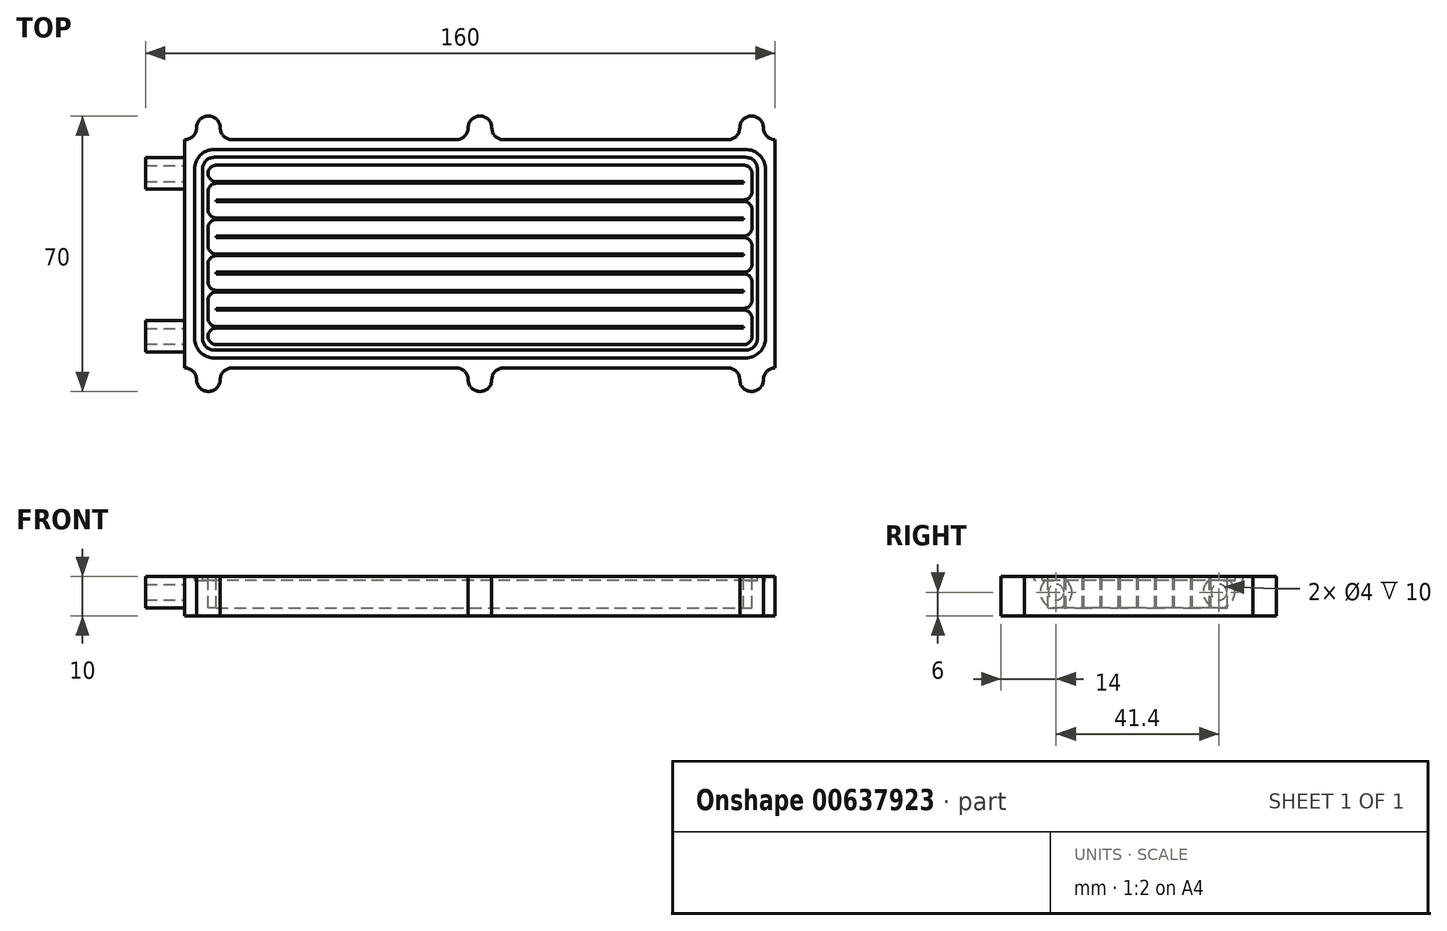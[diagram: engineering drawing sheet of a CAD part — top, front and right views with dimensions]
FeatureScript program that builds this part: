
annotation { "Feature Type Name" : "Feature", "Feature Type Description" : "" }
export const myFeature = defineFeature(function(context is Context, id is Id, definition is map)
    precondition{}
    {
        {
            var Q0;
            Q0=qCreatedBy(makeId("Top.planeOp"),FACE);
            var sketch = newSketch(context, id + "F0", { "sketchPlane" : qUnion([Q0])});
            skLineSegment(sketch, "E0.bottom", {"start": v(63, 29) * mm, "end": v(6, 29) * mm});
            skLineSegment(sketch, "E0.top", {"start": v(63, -29) * mm, "end": v(6, -29) * mm});
            skLineSegment(sketch, "E0.left", {"start": v(75, 29) * mm, "end": v(75, -29) * mm});
            skLineSegment(sketch, "E0.right", {"start": v(-75, 29) * mm, "end": v(-75, -29) * mm});
            skPoint(sketch, "E0.middle", {"position": v(0, 0) * mm});
            skArc(sketch, "E1", {"start": v(3, 32) * mm, "mid": v(0, 35) * mm, "end": v(-3, 32) * mm});
            skArc(sketch, "E2", {"start": v(-66, 32) * mm, "mid": v(-69, 35) * mm, "end": v(-72, 32) * mm});
            skArc(sketch, "E3", {"start": v(72, 32) * mm, "mid": v(69, 35) * mm, "end": v(66, 32) * mm});
            skArc(sketch, "E4", {"start": v(-75, 29) * mm, "mid": v(-72.88, 29.88) * mm, "end": v(-72, 32) * mm});
            skArc(sketch, "E5", {"start": v(-66, 32) * mm, "mid": v(-65.12, 29.88) * mm, "end": v(-63, 29) * mm});
            skArc(sketch, "E6", {"start": v(3, 32) * mm, "mid": v(3.88, 29.88) * mm, "end": v(6, 29) * mm});
            skArc(sketch, "E7", {"start": v(-6, 29) * mm, "mid": v(-3.88, 29.88) * mm, "end": v(-3, 32) * mm});
            skLineSegment(sketch, "E8.trimOffspring", {"start": v(-6, 29) * mm, "end": v(-63, 29) * mm});
            skArc(sketch, "E9", {"start": v(72, 32) * mm, "mid": v(72.88, 29.88) * mm, "end": v(75, 29) * mm});
            skArc(sketch, "E10", {"start": v(63, 29) * mm, "mid": v(65.12, 29.88) * mm, "end": v(66, 32) * mm});
            skArc(sketch, "E11.MirrorCS", {"start": v(-66, -32) * mm, "mid": v(-69, -35) * mm, "end": v(-72, -32) * mm});
            skArc(sketch, "E12.MirrorCS", {"start": v(-75, -29) * mm, "mid": v(-72.88, -29.88) * mm, "end": v(-72, -32) * mm});
            skArc(sketch, "E13.MirrorCS", {"start": v(-66, -32) * mm, "mid": v(-65.12, -29.88) * mm, "end": v(-63, -29) * mm});
            skArc(sketch, "E14.MirrorCS", {"start": v(-6, -29) * mm, "mid": v(-3.88, -29.88) * mm, "end": v(-3, -32) * mm});
            skArc(sketch, "E15.MirrorCS", {"start": v(3, -32) * mm, "mid": v(3.88, -29.88) * mm, "end": v(6, -29) * mm});
            skArc(sketch, "E16.MirrorCS", {"start": v(3, -32) * mm, "mid": v(0, -35) * mm, "end": v(-3, -32) * mm});
            skArc(sketch, "E17.MirrorCS", {"start": v(63, -29) * mm, "mid": v(65.12, -29.88) * mm, "end": v(66, -32) * mm});
            skArc(sketch, "E18.MirrorCS", {"start": v(72, -32) * mm, "mid": v(69, -35) * mm, "end": v(66, -32) * mm});
            skArc(sketch, "E19.MirrorCS", {"start": v(72, -32) * mm, "mid": v(72.88, -29.88) * mm, "end": v(75, -29) * mm});
            skLineSegment(sketch, "E20.trimOffspring", {"start": v(-6, -29) * mm, "end": v(-63, -29) * mm});
            skPoint(sketch, "E21.orphan", {"position": v(-75, 0) * mm});
            skPoint(sketch, "E22.end.orphan", {"position": v(75, 0) * mm});
            skSolve(sketch);
        }
        {
            var Q0;
            Q0=makeQuery(id+"F0.imprint","IMPRINT",FACE,{"disambiguationData":[TD([[makeQuery(id+"F0.imprint","IMPRINT",EDGE,{"derivedFrom":sQuery(id+"F0.wireOp",EDGE,"E0.bottom")}),1.0]])]});
            extrude(context, id + "F1", {"entities" : qUnion([Q0]), "oppositeDirection" : true, "depth" : 10 * mm, "offsetDistance" : 25 * mm});
        }
        {
            var Q0;
            Q0=makeQuery(id+"F1.opExtrude","CAP_FACE",FACE,{"disambiguationData":[OSD([sQuery(id+"F0.wireOp",EDGE,"E0.bottom"),sQuery(id+"F0.wireOp",EDGE,"E0.top"),sQuery(id+"F0.wireOp",EDGE,"E0.left"),sQuery(id+"F0.wireOp",EDGE,"E0.right")])],"isStart":true});
            var sketch = newSketch(context, id + "F2", { "sketchPlane" : qUnion([Q0])});
            skLineSegment(sketch, "E23.bottom", {"start": v(67.5, 26.5) * mm, "end": v(-67.5, 26.5) * mm});
            skLineSegment(sketch, "E23.top", {"start": v(67.5, -26.5) * mm, "end": v(-67.5, -26.5) * mm});
            skLineSegment(sketch, "E23.left", {"start": v(72.5, 21.5) * mm, "end": v(72.5, -21.5) * mm});
            skLineSegment(sketch, "E23.right", {"start": v(-72.5, 21.5) * mm, "end": v(-72.5, -21.5) * mm});
            skPoint(sketch, "E23.middle", {"position": v(0, 0) * mm});
            skPoint(sketch, "E24.visualSharp", {"position": v(-72.5, 26.5) * mm});
            skArc(sketch, "E24.filletArc", {"start": v(-67.5, 26.5) * mm, "mid": v(-71.04, 25.04) * mm, "end": v(-72.5, 21.5) * mm});
            skPoint(sketch, "E25.visualSharp", {"position": v(-72.5, -26.5) * mm});
            skArc(sketch, "E25.filletArc", {"start": v(-72.5, -21.5) * mm, "mid": v(-71.04, -25.04) * mm, "end": v(-67.5, -26.5) * mm});
            skPoint(sketch, "E26.visualSharp", {"position": v(72.5, -26.5) * mm});
            skArc(sketch, "E26.filletArc", {"start": v(67.5, -26.5) * mm, "mid": v(71.04, -25.04) * mm, "end": v(72.5, -21.5) * mm});
            skPoint(sketch, "E27.visualSharp", {"position": v(72.5, 26.5) * mm});
            skArc(sketch, "E27.filletArc", {"start": v(72.5, 21.5) * mm, "mid": v(71.04, 25.04) * mm, "end": v(67.5, 26.5) * mm});
            skLineSegment(sketch, "E28.0", {"start": v(67.5, 24.5) * mm, "end": v(-67.5, 24.5) * mm});
            skLineSegment(sketch, "E28.1", {"start": v(70.5, 21.5) * mm, "end": v(70.5, -21.5) * mm});
            skLineSegment(sketch, "E28.2", {"start": v(67.5, -24.5) * mm, "end": v(-67.5, -24.5) * mm});
            skLineSegment(sketch, "E28.3", {"start": v(-70.5, 21.5) * mm, "end": v(-70.5, -21.5) * mm});
            skPoint(sketch, "E29.visualSharp", {"position": v(-70.5, 24.5) * mm});
            skArc(sketch, "E29.filletArc", {"start": v(-67.5, 24.5) * mm, "mid": v(-69.62, 23.62) * mm, "end": v(-70.5, 21.5) * mm});
            skPoint(sketch, "E30.visualSharp", {"position": v(-70.5, -24.5) * mm});
            skArc(sketch, "E30.filletArc", {"start": v(-70.5, -21.5) * mm, "mid": v(-69.62, -23.62) * mm, "end": v(-67.5, -24.5) * mm});
            skPoint(sketch, "E31.visualSharp", {"position": v(70.5, 24.5) * mm});
            skArc(sketch, "E31.filletArc", {"start": v(70.5, 21.5) * mm, "mid": v(69.62, 23.62) * mm, "end": v(67.5, 24.5) * mm});
            skPoint(sketch, "E32.visualSharp", {"position": v(70.5, -24.5) * mm});
            skArc(sketch, "E32.filletArc", {"start": v(67.5, -24.5) * mm, "mid": v(69.62, -23.62) * mm, "end": v(70.5, -21.5) * mm});
            skSolve(sketch);
        }
        {
            var Q0;
            Q0 = qSketchRegion(id + "F2", true);
            extrude(context, id + "F3", {"entities" : qUnion([Q0]), "operationType" : NewBodyOperationType.REMOVE, "oppositeDirection" : true, "depth" : 1 * mm, "offsetDistance" : 25 * mm});
        }
        {
            var Q0;
            Q0=makeQuery(id+"F3.boolean.opBoolean","SPLIT",FACE,{"disambiguationData":[TD([makeQuery(id+"F3.opExtrude","SWEPT_FACE",FACE,{"disambiguationData":[OSD([sQuery(id+"F2.wireOp",EDGE,"E28.0")])]})])],"derivedFrom":makeQuery(id+"F1.opExtrude","CAP_FACE",FACE,{"disambiguationData":[OSD([sQuery(id+"F0.wireOp",EDGE,"E0.bottom"),sQuery(id+"F0.wireOp",EDGE,"E0.top"),sQuery(id+"F0.wireOp",EDGE,"E0.left"),sQuery(id+"F0.wireOp",EDGE,"E0.right")])],"isStart":true})});
            var sketch = newSketch(context, id + "F4", { "sketchPlane" : qUnion([Q0])});
            skArc(sketch, "E33", {"start": v(-67, -18.9) * mm, "mid": v(-69.1, -21) * mm, "end": v(-67, -23.1) * mm});
            skArc(sketch, "E34", {"start": v(67, -23.1) * mm, "mid": v(68.48, -22.48) * mm, "end": v(69.1, -21) * mm});
            skLineSegment(sketch, "E35", {"start": v(-67, -23.1) * mm, "end": v(67, -23.1) * mm});
            skLineSegment(sketch, "E36", {"start": v(67, -18.9) * mm, "end": v(-67, -18.9) * mm});
            skArc(sketch, "E37.0.1.0", {"start": v(-69.1, -16.4) * mm, "mid": v(-68.48, -17.88) * mm, "end": v(-67, -18.5) * mm});
            skArc(sketch, "E37.0.1.1", {"start": v(69.1, -16.4) * mm, "mid": v(68.48, -14.92) * mm, "end": v(67, -14.3) * mm});
            skLineSegment(sketch, "E37.0.1.2", {"start": v(-67, -18.5) * mm, "end": v(67, -18.5) * mm});
            skLineSegment(sketch, "E37.0.1.3", {"start": v(67, -14.3) * mm, "end": v(-67, -14.3) * mm});
            skArc(sketch, "E37.0.2.0", {"start": v(-67, -9.7) * mm, "mid": v(-68.48, -10.32) * mm, "end": v(-69.1, -11.8) * mm});
            skArc(sketch, "E37.0.2.1", {"start": v(67, -13.9) * mm, "mid": v(68.48, -13.28) * mm, "end": v(69.1, -11.8) * mm});
            skLineSegment(sketch, "E37.0.2.2", {"start": v(-67, -13.9) * mm, "end": v(67, -13.9) * mm});
            skLineSegment(sketch, "E37.0.2.3", {"start": v(67, -9.7) * mm, "end": v(-67, -9.7) * mm});
            skArc(sketch, "E37.0.3.0", {"start": v(-69.1, -7.2) * mm, "mid": v(-68.48, -8.68) * mm, "end": v(-67, -9.3) * mm});
            skArc(sketch, "E37.0.3.1", {"start": v(69.1, -7.2) * mm, "mid": v(68.48, -5.72) * mm, "end": v(67, -5.1) * mm});
            skLineSegment(sketch, "E37.0.3.2", {"start": v(-67, -9.3) * mm, "end": v(67, -9.3) * mm});
            skLineSegment(sketch, "E37.0.3.3", {"start": v(67, -5.1) * mm, "end": v(-67, -5.1) * mm});
            skArc(sketch, "E37.0.4.0", {"start": v(-67, -0.5) * mm, "mid": v(-68.48, -1.12) * mm, "end": v(-69.1, -2.6) * mm});
            skArc(sketch, "E37.0.4.1", {"start": v(67, -4.7) * mm, "mid": v(68.48, -4.08) * mm, "end": v(69.1, -2.6) * mm});
            skLineSegment(sketch, "E37.0.4.2", {"start": v(-67, -4.7) * mm, "end": v(67, -4.7) * mm});
            skLineSegment(sketch, "E37.0.4.3", {"start": v(67, -0.5) * mm, "end": v(-67, -0.5) * mm});
            skArc(sketch, "E37.0.5.0", {"start": v(-69.1, 2) * mm, "mid": v(-68.48, 0.52) * mm, "end": v(-67, -0.1) * mm});
            skArc(sketch, "E37.0.5.1", {"start": v(69.1, 2) * mm, "mid": v(68.48, 3.48) * mm, "end": v(67, 4.1) * mm});
            skLineSegment(sketch, "E37.0.5.2", {"start": v(-67, -0.1) * mm, "end": v(67, -0.1) * mm});
            skLineSegment(sketch, "E37.0.5.3", {"start": v(67, 4.1) * mm, "end": v(-67, 4.1) * mm});
            skArc(sketch, "E37.0.6.0", {"start": v(-67, 8.7) * mm, "mid": v(-68.48, 8.08) * mm, "end": v(-69.1, 6.6) * mm});
            skArc(sketch, "E37.0.6.1", {"start": v(67, 4.5) * mm, "mid": v(68.48, 5.12) * mm, "end": v(69.1, 6.6) * mm});
            skLineSegment(sketch, "E37.0.6.2", {"start": v(-67, 4.5) * mm, "end": v(67, 4.5) * mm});
            skLineSegment(sketch, "E37.0.6.3", {"start": v(67, 8.7) * mm, "end": v(-67, 8.7) * mm});
            skArc(sketch, "E37.0.7.0", {"start": v(-69.1, 11.2) * mm, "mid": v(-68.48, 9.72) * mm, "end": v(-67, 9.1) * mm});
            skArc(sketch, "E37.0.7.1", {"start": v(69.1, 11.2) * mm, "mid": v(68.48, 12.68) * mm, "end": v(67, 13.3) * mm});
            skLineSegment(sketch, "E37.0.7.2", {"start": v(-67, 9.1) * mm, "end": v(67, 9.1) * mm});
            skLineSegment(sketch, "E37.0.7.3", {"start": v(67, 13.3) * mm, "end": v(-67, 13.3) * mm});
            skArc(sketch, "E37.0.8.0", {"start": v(-67, 17.9) * mm, "mid": v(-68.48, 17.28) * mm, "end": v(-69.1, 15.8) * mm});
            skArc(sketch, "E37.0.8.1", {"start": v(67, 13.7) * mm, "mid": v(68.48, 14.32) * mm, "end": v(69.1, 15.8) * mm});
            skLineSegment(sketch, "E37.0.8.2", {"start": v(-67, 13.7) * mm, "end": v(67, 13.7) * mm});
            skLineSegment(sketch, "E37.0.8.3", {"start": v(67, 17.9) * mm, "end": v(-67, 17.9) * mm});
            skArc(sketch, "E37.0.9.0", {"start": v(-67, 22.5) * mm, "mid": v(-69.1, 20.4) * mm, "end": v(-67, 18.3) * mm});
            skArc(sketch, "E37.0.9.1", {"start": v(69.1, 20.4) * mm, "mid": v(68.48, 21.88) * mm, "end": v(67, 22.5) * mm});
            skLineSegment(sketch, "E37.0.9.2", {"start": v(-67, 18.3) * mm, "end": v(67, 18.3) * mm});
            skLineSegment(sketch, "E37.0.9.3", {"start": v(67, 22.5) * mm, "end": v(-67, 22.5) * mm});
            skLineSegment(sketch, "E37.direction1", {"start": v(-67, -23.1) * mm, "end": v(-42, -23.1) * mm, "construction": true});
            skLineSegment(sketch, "E37.direction2", {"start": v(-67, -23.1) * mm, "end": v(-67, -21) * mm, "construction": true});
            skLineSegment(sketch, "E38", {"start": v(-69.1, 15.8) * mm, "end": v(-69.1, 11.2) * mm});
            skLineSegment(sketch, "E39", {"start": v(69.1, 20.4) * mm, "end": v(69.1, 15.8) * mm});
            skLineSegment(sketch, "E40", {"start": v(67, -18.9) * mm, "end": v(67, -18.5) * mm});
            skLineSegment(sketch, "E41.trimOffspring", {"start": v(-67, -14.3) * mm, "end": v(-67, -13.9) * mm});
            skLineSegment(sketch, "E42", {"start": v(67, -9.3) * mm, "end": v(67, -9.7) * mm});
            skLineSegment(sketch, "E43.trimOffspring", {"start": v(67, -0.1) * mm, "end": v(67, -0.5) * mm});
            skLineSegment(sketch, "E44.trimOffspring", {"start": v(67, 9.1) * mm, "end": v(67, 8.7) * mm});
            skLineSegment(sketch, "E45.trimOffspring", {"start": v(67, 18.3) * mm, "end": v(67, 17.9) * mm});
            skLineSegment(sketch, "E46.trimOffspring", {"start": v(-67, 4.1) * mm, "end": v(-67, 4.5) * mm});
            skLineSegment(sketch, "E47.trimOffspring", {"start": v(-67, 13.3) * mm, "end": v(-67, 13.7) * mm});
            skPoint(sketch, "E48.orphan", {"position": v(-69.1, -21) * mm});
            skLineSegment(sketch, "E49.trimOffspring", {"start": v(-69.1, -11.8) * mm, "end": v(-69.1, -16.4) * mm});
            skLineSegment(sketch, "E50.trimOffspring", {"start": v(-69.1, -2.6) * mm, "end": v(-69.1, -7.2) * mm});
            skLineSegment(sketch, "E51.trimOffspring", {"start": v(-69.1, 6.6) * mm, "end": v(-69.1, 2) * mm});
            skLineSegment(sketch, "E52.trimOffspring", {"start": v(69.1, 11.2) * mm, "end": v(69.1, 6.6) * mm});
            skLineSegment(sketch, "E53.trimOffspring", {"start": v(69.1, 2) * mm, "end": v(69.1, -2.6) * mm});
            skLineSegment(sketch, "E54.trimOffspring", {"start": v(69.1, -7.2) * mm, "end": v(69.1, -11.8) * mm});
            skLineSegment(sketch, "E55.trimOffspring", {"start": v(69.1, -16.4) * mm, "end": v(69.1, -21) * mm});
            skLineSegment(sketch, "E56", {"start": v(-67, -4.7) * mm, "end": v(-67, -5.1) * mm});
            skSolve(sketch);
        }
        {
            var Q0;
            Q0 = qSketchRegion(id + "F4", true);
            extrude(context, id + "F5", {"entities" : qUnion([Q0]), "operationType" : NewBodyOperationType.REMOVE, "oppositeDirection" : true, "depth" : 8 * mm, "offsetDistance" : 25 * mm});
        }
        {
            var Q0;
            Q0=makeQuery(id+"F1.opExtrude","SWEPT_FACE",FACE,{"disambiguationData":[OSD([sQuery(id+"F0.wireOp",EDGE,"E0.right")])]});
            var sketch = newSketch(context, id + "F6", { "sketchPlane" : qUnion([Q0])});
            skCircle(sketch, "E57", {"center": v(-20.4, -4) * mm, "radius": 2 * mm});
            skCircle(sketch, "E58", {"center": v(-20.4, -4) * mm, "radius": 4 * mm});
            skCircle(sketch, "E59", {"center": v(21, -4) * mm, "radius": 2 * mm});
            skCircle(sketch, "E60", {"center": v(21, -4) * mm, "radius": 4 * mm});
            skSolve(sketch);
        }
        {
            var Q0;
            Q0 = qSketchRegion(id + "F6", true);
            extrude(context, id + "F7", {"entities" : qUnion([Q0]), "operationType" : NewBodyOperationType.ADD, "depth" : 10 * mm, "offsetDistance" : 25 * mm});
        }
    });
